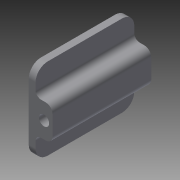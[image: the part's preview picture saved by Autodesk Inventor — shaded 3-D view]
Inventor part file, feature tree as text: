
AUTODESK INVENTOR PART (.ipt)
format: ipt  version: 2015 (Build 190159000, 159)  size: 137,216 bytes
history: native  units: in
note: dims shown in document units (in); Inventor stores cm internally (conversion verified against a paired STEP export)
features: extrude x4, sketch x4, fillet x3, projected_geometry x2
ambient origin geometry x8: Origin, YZ Plane, XZ Plane, XY Plane, X Axis, Y Axis, Z Axis, Center Point
bodies: Solid1 (feature_tree)
feature tree (13):
  extrude  "Extrusion1"  Depth=1.815in
  extrude  "Extrusion2"  Depth=0.125in TaperAngle=0.0deg
  extrude  "Extrusion3"  Depth=0.3125in
  extrude  "Extrusion4"  Depth=0.125in
  fillet  "Fillet1"  Radius=0.1in
  fillet  "Fillet2"  Radius=0.225in
  fillet  "Fillet4"  Radius=0.1406in
  sketch  "Sketch1"  dims[d0=1.5in d1=1.815in]
  sketch  "Sketch2"  dims[d2=0.125in d3=0.0in d5=0.125in d6=0.0in]
  projected_geometry  "Projected Loop1"
  sketch  "Sketch3"  dims[d7=0.3125in d8=0.0in d9=0.188in]
  sketch  "Sketch4"  dims[d10=2.0in d11=0.0in d12=0.125in d13=0.1in d15=0.225in d16=0.1406in]
  projected_geometry  "Projected Loop2"
